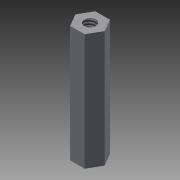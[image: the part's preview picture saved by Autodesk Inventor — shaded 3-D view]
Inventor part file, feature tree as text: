
AUTODESK INVENTOR PART (.ipt)
format: ipt  version: 2015 (Build 190159000, 159)  size: 82,432 bytes
history: native  units: in
note: dims shown in document units (in); Inventor stores cm internally (conversion verified against a paired STEP export)
features: sketch x2, extrude x1, hole x1, projected_geometry x1
ambient origin geometry x8: Origin, YZ Plane, XZ Plane, XY Plane, X Axis, Y Axis, Z Axis, Center Point
bodies: Solid1 (feature_tree)
feature tree (5):
  extrude  "Extrusion1"  Depth=0.1083in
  hole  "Hole1"  [1 undecoded]
  sketch  "Sketch2"  dims[d0=0.25in d1=0.1083in]
  sketch  "Sketch3"  dims[d2=1.0in d3=0.0in d4=0.098in d5=1.0in d6=0.375in d7=0.25in d8=0.5635in d9=0.375in d10=0.8108in]
  projected_geometry  "Projected Loop1"
note: 1 required parameter value undecoded (feature->parameter linkage not recoverable at this tier; creation-order binding heuristic only, values carry confidence <= 0.55)
